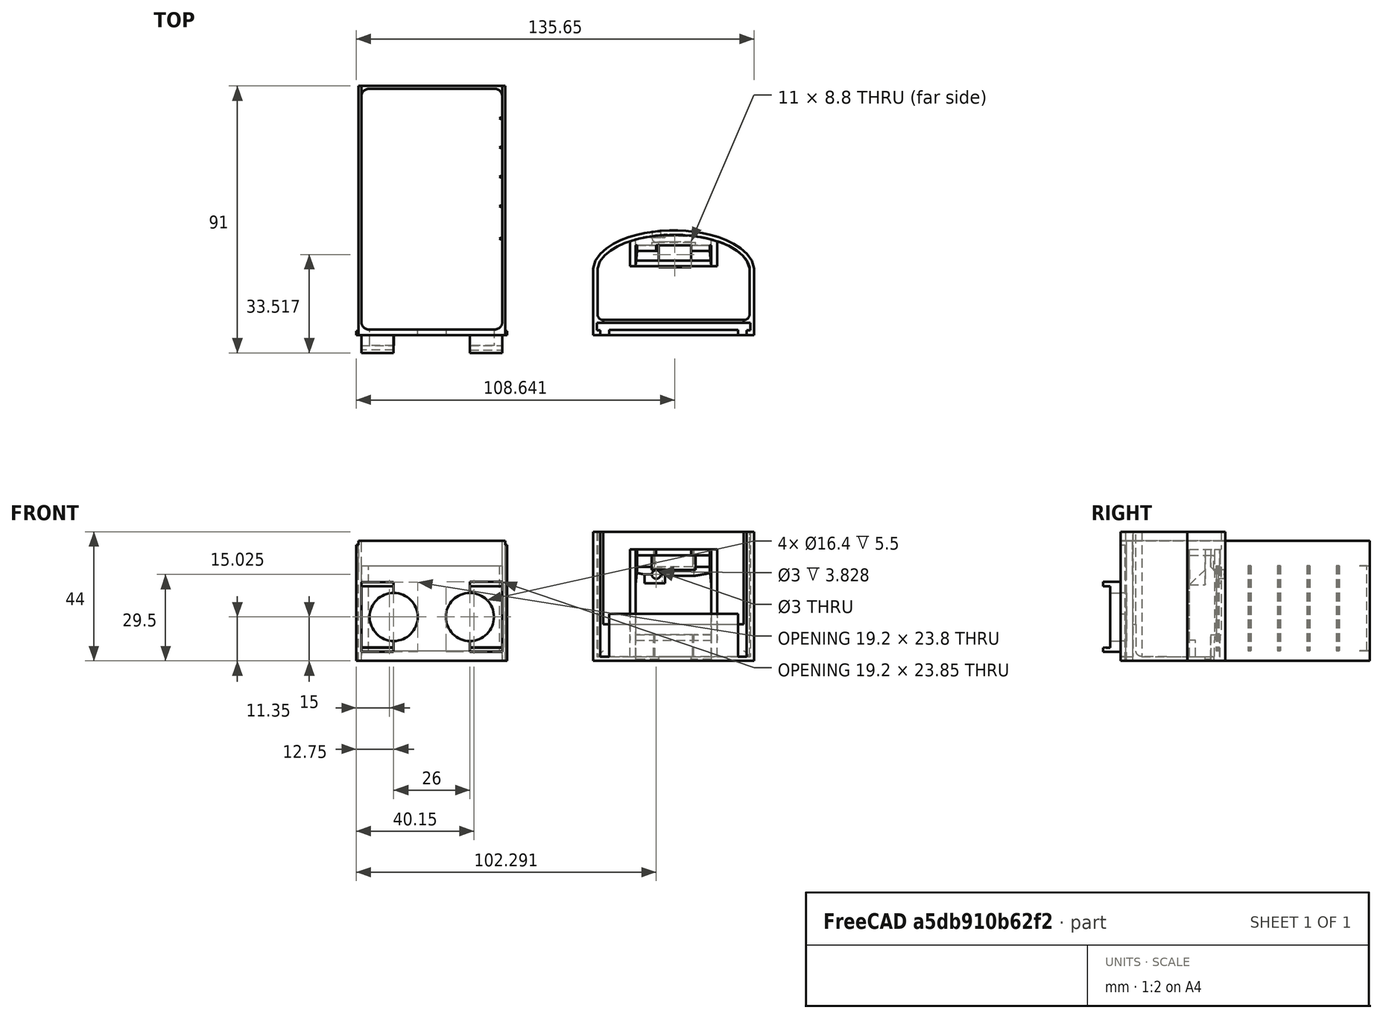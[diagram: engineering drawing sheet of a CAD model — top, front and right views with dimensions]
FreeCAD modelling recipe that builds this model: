
FCSTD DOCUMENT  (FreeCAD 0.18.4R)
Label: sonic.sensor.V5
License: All rights reserved
LicenseURL: http://en.wikipedia.org/wiki/All_rights_reserved
objects: Part::Extrusion×56, Part::Feature×45, Part::Part2DObjectPython×29, Part::Cut×25, Part::MultiFuse×17, Part::FeaturePython×8, App::DocumentObjectGroup×4
note: 180 computed .brp shape members not serialized (recipe doc carries the construction recipe); baked Part::Feature solids carry a one-line shape summary decoded from their .brp

FEATURE [Part::Feature] Extrusion004
  Placement = pos=(0,4e-15,-3.5) rot=(0,0,1;0rad)
  shape: bbox 47.9 x 2.5 x 34.5 mm, 6 faces (baked)
FEATURE [Part::Part2DObjectPython] Rectangle007  # Draft 2D object (typed FeaturePython)
  ChamferSize = 0
  Columns = 1
  FilletRadius = 0
  Height = 2.5
  Length = 0.2
  MakeFace = true
  Placement = pos=(133.392,-28.2833,50) rot=(0,0,1;0rad)
  Rows = 1
FEATURE [Part::Part2DObjectPython] Rectangle  # Draft 2D object (typed FeaturePython)
  ChamferSize = 0
  Columns = 1
  FilletRadius = 0
  Height = 50
  Length = 54.9181
  MakeFace = true
  Placement = pos=(79.9819,-14.25,-6e-15) rot=(1,0,0;1.5708rad)
  Rows = 1
FEATURE [Part::Feature] Face
  shape: bbox 51.9 x 2e-07 x 45.5 mm, 1 faces, 0 solids (baked)
FEATURE [Part::Feature] Slice_child  label="Slice.003"
  Placement = pos=(0,5,0) rot=(0,0,1;0rad)
  shape: bbox 54.92 x 13.01 x 50 mm, 74 faces (baked)
FEATURE [Part::Extrusion] Extrusion
  Base = -> Rectangle
  Dir = (-1.25e-14,-15.75,-2.1e-14)
  DirMode = 0
  FaceMakerClass = Part::FaceMakerBullseye
  LengthFwd = 0
  LengthRev = 0
  Solid = true
  Symmetric = false
FEATURE [Part::Part2DObjectPython] Rectangle004  # Draft 2D object (typed FeaturePython)
  ChamferSize = 0
  Columns = 1
  FilletRadius = 0
  Height = 14.5
  Length = 43.9024
  MakeFace = true
  Placement = pos=(85.4897,-30,1.5) rot=(1,0,0;1.5708rad)
  Rows = 1
FEATURE [Part::Part2DObjectPython] Rectangle002  # Draft 2D object (typed FeaturePython)
  ChamferSize = 0
  Columns = 1
  FilletRadius = 0
  Height = 2.5
  Length = 51.9024
  MakeFace = true
  Placement = pos=(81.4897,-25.7833,47) rot=(0,0,1;0rad)
  Rows = 1
FEATURE [Part::Extrusion] Extrusion002
  Base = -> Rectangle002
  Dir = (0,9.1e-14,-45.5)
  DirMode = 0
  FaceMakerClass = Part::FaceMakerBullseye
  LengthFwd = 0
  LengthRev = 0
  Solid = true
  Symmetric = false
FEATURE [Part::Cut] Cut001
  Base = -> Extrusion002
  Tool = -> Extrusion004
FEATURE [Part::Part2DObjectPython] Rectangle005  # Draft 2D object (typed FeaturePython)
  ChamferSize = 0
  Columns = 1
  FilletRadius = 0
  Height = 1.71667
  Length = 1
  MakeFace = true
  Placement = pos=(132.392,-30,47) rot=(0,0,1;0rad)
  Rows = 1
FEATURE [Part::Extrusion] Extrusion007
  Base = -> Rectangle005
  Dir = (-1.616e-13,1.397e-13,-45.5)
  DirMode = 0
  FaceMakerClass = Part::FaceMakerBullseye
  LengthFwd = 0
  LengthRev = 0
  Solid = true
  Symmetric = false
FEATURE [Part::Extrusion] Extrusion006
  Base = -> Rectangle004
  Dir = (-1.38e-14,1.81667,-9.5e-15)
  DirMode = 0
  FaceMakerClass = Part::FaceMakerBullseye
  LengthFwd = 0
  LengthRev = 0
  Solid = true
  Symmetric = false
FEATURE [Part::Extrusion] Extrusion005
  Base = -> Face
  Dir = (0,-1.5,-3e-15)
  DirMode = 0
  FaceMakerClass = Part::FaceMakerBullseye
  LengthFwd = 0
  LengthRev = 0
  Solid = true
  Symmetric = false
FEATURE [Part::Part2DObjectPython] Rectangle001  # Draft 2D object (typed FeaturePython)
  ChamferSize = 0
  Columns = 1
  FilletRadius = 0
  Height = 48.5
  Length = 51.9024
  MakeFace = true
  Placement = pos=(81.4897,-14.25,1.5) rot=(1,0,0;1.5708rad)
  Rows = 1
FEATURE [Part::Extrusion] Extrusion001
  Base = -> Rectangle001
  Dir = (-1.25e-14,-15.75,-2.1e-14)
  DirMode = 0
  FaceMakerClass = Part::FaceMakerBullseye
  LengthFwd = 0
  LengthRev = 0
  Solid = true
  Symmetric = false
FEATURE [Part::Cut] Cut
  Base = -> Extrusion
  Tool = -> Extrusion001
FEATURE [Part::Feature] Face001
  shape: bbox 54.92 x 2e-07 x 50 mm, 1 faces, 0 solids (baked)
FEATURE [Part::Feature] Extrusion010
  Placement = pos=(-52.1024,4.6e-14,-2.8e-14) rot=(0,0,1;0rad)
  shape: bbox 0.2 x 2.5 x 48.5 mm, 6 faces (baked)
FEATURE [Part::Cut] Cut002
  Base = -> Cut001
  Tool = -> Extrusion005
FEATURE [Part::MultiFuse] Fusion
  Shapes = -> [Cut,Cut002,Extrusion006]
FEATURE [Part::Part2DObjectPython] Rectangle006  # Draft 2D object (typed FeaturePython)
  ChamferSize = 0
  Columns = 1
  FilletRadius = 0
  Height = 1
  Length = 1.71667
  MakeFace = true
  Placement = pos=(81.4897,-28.2833,47) rot=(0,0,-1;1.5708rad)
  Rows = 1
FEATURE [Part::Extrusion] Extrusion008
  Base = -> Rectangle006
  Dir = (-4.87e-14,1.397e-13,-45.5)
  DirMode = 0
  FaceMakerClass = Part::FaceMakerBullseye
  LengthFwd = 0
  LengthRev = 0
  Solid = true
  Symmetric = false
FEATURE [Part::MultiFuse] Fusion001
  Shapes = -> [Fusion,Extrusion008,Extrusion007]
FEATURE [Part::Extrusion] Extrusion009
  Base = -> Rectangle007
  Dir = (0,7.3e-15,-48.5)
  DirMode = 0
  FaceMakerClass = Part::FaceMakerBullseye
  LengthFwd = 0
  LengthRev = 0
  Solid = true
  Symmetric = false
FEATURE [Part::Cut] Cut003
  Base = -> Fusion001
  Tool = -> Extrusion009
FEATURE [Part::Cut] Cut004
  Base = -> Cut003
  Tool = -> Extrusion010
FEATURE [Part::Part2DObjectPython] Rectangle009  # Draft 2D object (typed FeaturePython)
  ChamferSize = 0
  Columns = 1
  FilletRadius = 0
  Height = 2
  Length = 2
  MakeFace = true
  Placement = pos=(133.392,-22.7833,1.5) rot=(0.57735,-0.57735,-0.57735;2.0944rad)
  Rows = 1
FEATURE [Part::Extrusion] Extrusion011
  Base = -> Rectangle009
  Dir = (-51.9024,0,0)
  DirMode = 0
  FaceMakerClass = Part::FaceMakerBullseye
  LengthFwd = 0
  LengthRev = 0
  Solid = true
  Symmetric = false
FEATURE [Part::Part2DObjectPython] Circle  # Draft 2D object (typed FeaturePython)
  FirstAngle = 0
  LastAngle = 0
  MakeFace = true
  Placement = pos=(81.4897,-22.7833,3.5) rot=(0.57735,-0.57735,-0.57735;2.0944rad)
  Radius = 2
  Support = -> [Extrusion011]
FEATURE [Part::Extrusion] Extrusion012
  Base = -> Circle
  Dir = (51.9024,0,0)
  DirMode = 0
  FaceMakerClass = Part::FaceMakerBullseye
  LengthFwd = 0
  LengthRev = 0
  Solid = true
  Symmetric = false
FEATURE [Part::Cut] Cut005
  Base = -> Extrusion011
  Tool = -> Extrusion012
FEATURE [Part::MultiFuse] Fusion002
  Shapes = -> [Cut004,Cut005]
FEATURE [Part::Part2DObjectPython] Rectangle010  # Draft 2D object (typed FeaturePython)
  ChamferSize = 0
  Columns = 1
  FilletRadius = 0
  Height = 2.00245
  Length = 2
  MakeFace = true
  Placement = pos=(133.392,-24.7833,47) rot=(0,0,1;1.5708rad)
  Rows = 1
FEATURE [Part::Extrusion] Extrusion013
  Base = -> Rectangle010
  Dir = (1.161e-13,2.071e-13,-45.5)
  DirMode = 0
  FaceMakerClass = Part::FaceMakerBullseye
  LengthFwd = 0
  LengthRev = 0
  Solid = true
  Symmetric = false
FEATURE [Part::Part2DObjectPython] Circle001  # Draft 2D object (typed FeaturePython)
  FirstAngle = 0
  LastAngle = 0
  MakeFace = true
  Placement = pos=(131.39,-22.7833,47) rot=(0,0,1;1.5708rad)
  Radius = 2
  Support = -> [Extrusion013]
FEATURE [Part::Extrusion] Extrusion014
  Base = -> Circle001
  Dir = (3.53e-14,2.425e-13,-45.5)
  DirMode = 0
  FaceMakerClass = Part::FaceMakerBullseye
  LengthFwd = 0
  LengthRev = 0
  Solid = true
  Symmetric = false
FEATURE [Part::Cut] Cut006
  Base = -> Extrusion013
  Tool = -> Extrusion014
FEATURE [Part::Part2DObjectPython] Rectangle012  # Draft 2D object (typed FeaturePython)
  ChamferSize = 0
  Columns = 1
  FilletRadius = 0
  Height = 2
  Length = 2
  MakeFace = true
  Placement = pos=(83.4897,-24.7833,47) rot=(0,0,1;1.5708rad)
  Rows = 1
  Support = -> [Fusion002]
FEATURE [Part::Extrusion] Extrusion015
  Base = -> Rectangle012
  Dir = (1.161e-13,2.071e-13,-45.5)
  DirMode = 0
  FaceMakerClass = Part::FaceMakerBullseye
  LengthFwd = 0
  LengthRev = 0
  Solid = true
  Symmetric = false
FEATURE [Part::Part2DObjectPython] Circle002  # Draft 2D object (typed FeaturePython)
  FirstAngle = 0
  LastAngle = 0
  MakeFace = true
  Placement = pos=(83.4897,-22.7833,47) rot=(0,0,1;1.5708rad)
  Radius = 2
  Support = -> [Extrusion015]
FEATURE [Part::Extrusion] Extrusion016
  Base = -> Circle002
  Dir = (3.53e-14,2.425e-13,-45.5)
  DirMode = 0
  FaceMakerClass = Part::FaceMakerBullseye
  LengthFwd = 0
  LengthRev = 0
  Solid = true
  Symmetric = false
FEATURE [Part::Cut] Cut007
  Base = -> Extrusion015
  Tool = -> Extrusion016
FEATURE [Part::MultiFuse] Fusion003
  Shapes = -> [Cut007,Fusion002,Cut006]
FEATURE [Part::Extrusion] Extrusion017
  Base = -> Face001
  Dir = (4e-15,5,6.7e-15)
  DirMode = 0
  FaceMakerClass = Part::FaceMakerBullseye
  LengthFwd = 0
  LengthRev = 0
  Solid = true
  Symmetric = false
FEATURE [Part::MultiFuse] Fusion004
  Shapes = -> [Fusion003,Extrusion017,Slice_child]
FEATURE [Part::Feature] Fusion016
  Placement = pos=(4e-15,0,-5) rot=(0,0,1;0rad)
  shape: bbox 51.5 x 71 x 41 mm, 89 faces (baked)
FEATURE [Part::Part2DObjectPython] Rectangle019  # Draft 2D object (typed FeaturePython)
  ChamferSize = 0
  Columns = 1
  FilletRadius = 0
  Height = 6
  Length = 11
  MakeFace = true
  Placement = pos=(38,-30,6.8002) rot=(1,0,0;3.14159rad)
  Rows = 1
  Support = -> [Fusion016]
FEATURE [Part::Extrusion] Extrusion025
  Base = -> Rectangle019
  Dir = (0,0,-0.699902)
  DirMode = 0
  FaceMakerClass = Part::FaceMakerBullseye
  LengthFwd = 0
  LengthRev = 0
  Solid = true
  Symmetric = false
FEATURE [Part::Part2DObjectPython] Rectangle020  # Draft 2D object (typed FeaturePython)
  ChamferSize = 0
  Columns = 1
  FilletRadius = 0
  Height = 11
  Length = 6
  MakeFace = true
  Placement = pos=(12,-30,6.8002) rot=(0.707107,-0.707107,0;3.14159rad)
  Rows = 1
  Support = -> [Fusion016]
FEATURE [Part::Extrusion] Extrusion026
  Base = -> Rectangle020
  Dir = (0,0,-0.699902)
  DirMode = 0
  FaceMakerClass = Part::FaceMakerBullseye
  LengthFwd = 0
  LengthRev = 0
  Solid = true
  Symmetric = false
FEATURE [Part::Part2DObjectPython] Rectangle021  # Draft 2D object (typed FeaturePython)
  ChamferSize = 0
  Columns = 1
  FilletRadius = 0
  Height = 6
  Length = 11
  MakeFace = true
  Placement = pos=(49,-30,29.2) rot=(0,0,1;3.14159rad)
  Rows = 1
  Support = -> [Fusion016]
FEATURE [Part::Part2DObjectPython] Rectangle022  # Draft 2D object (typed FeaturePython)
  ChamferSize = 0
  Columns = 1
  FilletRadius = 0
  Height = 6
  Length = 11
  MakeFace = true
  Placement = pos=(12,-30,29.2) rot=(0,0,1;3.14159rad)
  Rows = 1
FEATURE [Part::Extrusion] Extrusion027
  Base = -> Rectangle022
  Dir = (0,0,0.699902)
  DirMode = 0
  FaceMakerClass = Part::FaceMakerBullseye
  LengthFwd = 0
  LengthRev = 0
  Solid = true
  Symmetric = false
FEATURE [Part::Extrusion] Extrusion028
  Base = -> Rectangle021
  Dir = (0,0,0.749176)
  DirMode = 0
  FaceMakerClass = Part::FaceMakerBullseye
  LengthFwd = 0
  LengthRev = 0
  Solid = true
  Symmetric = false
FEATURE [Part::MultiFuse] Fusion017
  Shapes = -> [Extrusion026,Extrusion025,Extrusion028,Extrusion027]
FEATURE [Part::MultiFuse] Fusion018
  Shapes = -> [Fusion016,Fusion017]
FEATURE [Part::Feature] Face002
  Placement = pos=(0,5,0) rot=(0,0,1;0rad)
  shape: bbox 1.002e-05 x 1.2 x 0.75 mm, 1 faces, 0 solids (baked)
FEATURE [Part::Extrusion] Extrusion029
  Base = -> Face002
  Dir = (0.2,0,0)
  DirMode = 0
  FaceMakerClass = Part::FaceMakerBullseye
  LengthFwd = 0
  LengthRev = 0
  Solid = true
  Symmetric = false
FEATURE [Part::Cut] Cut031
  Base = -> Fusion004
  Tool = -> Extrusion029
FEATURE [Part::Feature] Face003
  Placement = pos=(0,5,0) rot=(0,0,1;0rad)
  shape: bbox 1.002e-05 x 1.2 x 0.75 mm, 1 faces, 0 solids (baked)
FEATURE [Part::Extrusion] Extrusion030
  Base = -> Face003
  Dir = (-0.2,0,0)
  DirMode = 0
  FaceMakerClass = Part::FaceMakerBullseye
  LengthFwd = 0
  LengthRev = 0
  Solid = true
  Symmetric = false
FEATURE [Part::Cut] Cut032
  Base = -> Cut031
  Tool = -> Extrusion030
FEATURE [Part::Feature] Face004
  shape: bbox 8.9 x 1.8 x 1.002e-05 mm, 1 faces, 0 solids (baked)
FEATURE [Part::Extrusion] Extrusion031
  Base = -> Face004
  Dir = (0,0,-0.2)
  DirMode = 0
  FaceMakerClass = Part::FaceMakerBullseye
  LengthFwd = 0
  LengthRev = 0
  Solid = true
  Symmetric = false
FEATURE [Part::Cut] Cut033
  Base = -> Cut032
  Tool = -> Extrusion031
FEATURE [Part::Feature] Face005
  shape: bbox 0.2 x 1.2 x 1.002e-05 mm, 1 faces, 0 solids (baked)
FEATURE [Part::Extrusion] Extrusion032
  Base = -> Face005
  Dir = (0,0,-0.2)
  DirMode = 0
  FaceMakerClass = Part::FaceMakerBullseye
  LengthFwd = 0
  LengthRev = 0
  Solid = true
  Symmetric = false
FEATURE [Part::Cut] Cut034
  Base = -> Cut033
  Tool = -> Extrusion032
FEATURE [Part::Feature] Face006
  shape: bbox 8 x 1.8 x 1.002e-05 mm, 1 faces, 0 solids (baked)
FEATURE [Part::Extrusion] Extrusion033
  Base = -> Face006
  Dir = (0,0,-0.2)
  DirMode = 0
  FaceMakerClass = Part::FaceMakerBullseye
  LengthFwd = 0
  LengthRev = 0
  Solid = true
  Symmetric = false
FEATURE [Part::Cut] Cut035
  Base = -> Cut034
  Tool = -> Extrusion033
FEATURE [Part::Feature] Face007
  shape: bbox 0.2 x 1.2 x 1.002e-05 mm, 1 faces, 0 solids (baked)
FEATURE [Part::Extrusion] Extrusion034
  Base = -> Face007
  Dir = (0,0,-0.2)
  DirMode = 0
  FaceMakerClass = Part::FaceMakerBullseye
  LengthFwd = 0
  LengthRev = 0
  Solid = true
  Symmetric = false
FEATURE [Part::Cut] Cut036
  Base = -> Cut035
  Tool = -> Extrusion034
FEATURE [Part::Feature] Face008
  shape: bbox 8 x 1.002e-05 x 0.75 mm, 1 faces, 0 solids (baked)
FEATURE [Part::Extrusion] Extrusion035
  Base = -> Face008
  Dir = (0,-0.2,0)
  DirMode = 0
  FaceMakerClass = Part::FaceMakerBullseye
  LengthFwd = 0
  LengthRev = 0
  Solid = true
  Symmetric = false
FEATURE [Part::Feature] Face009
  shape: bbox 8 x 1.002e-05 x 0.2 mm, 1 faces, 0 solids (baked)
FEATURE [Part::Extrusion] Extrusion036
  Base = -> Face009
  Dir = (0,-0.2,0)
  DirMode = 0
  FaceMakerClass = Part::FaceMakerBullseye
  LengthFwd = 0
  LengthRev = 0
  Solid = true
  Symmetric = false
FEATURE [Part::Cut] Cut037
  Base = -> Cut036
  Tool = -> Extrusion035
FEATURE [Part::Cut] Cut038
  Base = -> Cut037
  Tool = -> Extrusion036
FEATURE [Part::Feature] Face010
  shape: bbox 8.9 x 1.002e-05 x 0.75 mm, 1 faces, 0 solids (baked)
FEATURE [Part::Extrusion] Extrusion037
  Base = -> Face010
  Dir = (0,-0.2,0)
  DirMode = 0
  FaceMakerClass = Part::FaceMakerBullseye
  LengthFwd = 0
  LengthRev = 0
  Solid = true
  Symmetric = false
FEATURE [Part::Feature] Face011
  shape: bbox 8.9 x 1.002e-05 x 0.2 mm, 1 faces, 0 solids (baked)
FEATURE [Part::Extrusion] Extrusion038
  Base = -> Face011
  Dir = (0,-0.2,0)
  DirMode = 0
  FaceMakerClass = Part::FaceMakerBullseye
  LengthFwd = 0
  LengthRev = 0
  Solid = true
  Symmetric = false
FEATURE [Part::Cut] Cut039
  Base = -> Cut038
  Tool = -> Extrusion037
FEATURE [Part::Cut] Cut040
  Base = -> Cut039
  Tool = -> Extrusion038
FEATURE [Part::Part2DObjectPython] Rectangle023  # Draft 2D object (typed FeaturePython)
  ChamferSize = 0
  Columns = 1
  FilletRadius = 0
  Height = 1.5
  Length = 0.75
  MakeFace = true
  Placement = pos=(-0.75,-30,41) rot=(0,0,1;0rad)
  Rows = 1
  Support = -> [Fusion018]
FEATURE [Part::Part2DObjectPython] Rectangle024  # Draft 2D object (typed FeaturePython)
  ChamferSize = 0
  Columns = 1
  FilletRadius = 0
  Height = 1.5
  Length = 0.75
  MakeFace = true
  Placement = pos=(50,-30,41) rot=(0,0,1;0rad)
  Rows = 1
FEATURE [Part::Extrusion] Extrusion039
  Base = -> Rectangle024
  Dir = (0,0,-1)
  DirMode = 0
  FaceMakerClass = Part::FaceMakerBullseye
  LengthFwd = 0
  LengthRev = 0
  Solid = true
  Symmetric = false
FEATURE [Part::Extrusion] Extrusion040
  Base = -> Rectangle023
  Dir = (0,0,-1)
  DirMode = 0
  FaceMakerClass = Part::FaceMakerBullseye
  LengthFwd = 0
  LengthRev = 0
  Solid = true
  Symmetric = false
FEATURE [Part::Cut] Cut041
  Base = -> Fusion018
  Tool = -> Extrusion039
FEATURE [Part::Cut] Cut042
  Base = -> Cut041
  Tool = -> Extrusion040
FEATURE [Part::Part2DObjectPython] Rectangle026  # Draft 2D object (typed FeaturePython)
  ChamferSize = 0
  Columns = 1
  FilletRadius = 0
  Height = 79.8861
  Length = 72.5841
  MakeFace = true
  Placement = pos=(-10.6149,-28,32.5) rot=(0,0,1;0rad)
  Rows = 1
  Support = -> [Cut042]
FEATURE [Part::Extrusion] Extrusion041
  Base = -> Rectangle026
  Dir = (0,0,70.6218)
  DirMode = 0
  FaceMakerClass = Part::FaceMakerBullseye
  LengthFwd = 0
  LengthRev = 0
  Solid = true
  Symmetric = false
FEATURE [Part::Cut] Cut043
  Base = -> Cut042
  Tool = -> Extrusion041
FEATURE [Part::Part2DObjectPython] Rectangle028  # Draft 2D object (typed FeaturePython)
  ChamferSize = 0
  Columns = 1
  FilletRadius = 0
  Height = 277.459
  Length = 179.893
  MakeFace = true
  Placement = pos=(-88.9464,2.9782,-138.729) rot=(1,0,0;1.5708rad)
  Rows = 1
  Support = -> [Cut043]
FEATURE [Part::FeaturePython] Slice  # WARN: FeaturePython — macro-defined, semantics opaque (R4)
  Base = -> Cut043
  Mode = 1
  Tolerance = 0
  Tools = -> [Rectangle028]
FEATURE [Part::FeaturePython] Slice_child0  label="Slice.0"  # WARN: FeaturePython — macro-defined, semantics opaque (R4)
  Base = -> Slice
  FilterType = 1
  Invert = false
  OverrideMaxVal = 0
  WindowFrom = 80
  WindowTo = 100
  items = 0
FEATURE [Part::Feature] Slice_child002  label="Slice.004"
  Placement = pos=(0,20,0) rot=(0,0,1;0rad)
  shape: bbox 50 x 32.02 x 32.5 mm, 17 faces (baked)
FEATURE [Part::Feature] Face012
  shape: bbox 1 x 6.243e-07 x 32.5 mm, 1 faces, 0 solids (baked)
FEATURE [Part::Extrusion] Extrusion042
  Base = -> Face012
  Dir = (6e-16,20,-4.4e-15)
  DirMode = 0
  FaceMakerClass = Part::FaceMakerBullseye
  LengthFwd = 0
  LengthRev = 0
  Solid = true
  Symmetric = false
FEATURE [Part::Feature] Face013
  shape: bbox 1 x 6.243e-07 x 32.5 mm, 1 faces, 0 solids (baked)
FEATURE [Part::Extrusion] Extrusion043
  Base = -> Face013
  Dir = (6e-16,20,-4.4e-15)
  DirMode = 0
  FaceMakerClass = Part::FaceMakerBullseye
  LengthFwd = 0
  LengthRev = 0
  Solid = true
  Symmetric = false
FEATURE [Part::MultiFuse] Fusion019
  Shapes = -> [Slice_child0,Extrusion042,Extrusion043,Slice_child002]
FEATURE [Part::Part2DObjectPython] Wire002  # Draft 2D object (typed FeaturePython)
  ChamferSize = 0
  Closed = true
  End = (49,43.5,32.5)
  FilletRadius = 0
  Length = 3.23607
  MakeFace = true
  Placement = pos=(49,44.5,32.5) rot=(0,0,1;0rad)
  Points = (3) [(0,0,0),(-1,-0.5,0),(0,-1,0)]
  Start = (49,44.5,32.5)
  Subdivisions = 0
FEATURE [Part::Extrusion] Extrusion044
  Base = -> Wire002
  Dir = (0,0,-32.5)
  DirMode = 0
  FaceMakerClass = Part::FaceMakerBullseye
  LengthFwd = 0
  LengthRev = 0
  Solid = true
  Symmetric = false
FEATURE [Part::Feature] Extrusion045
  Placement = pos=(7.1e-15,-10,-7.1e-15) rot=(0,0,1;0rad)
  shape: bbox 1 x 1 x 32.5 mm, 5 faces (baked)
FEATURE [Part::Feature] Extrusion046
  Placement = pos=(0,-30,0) rot=(0,0,1;0rad)
  shape: bbox 1 x 1 x 32.5 mm, 5 faces (baked)
FEATURE [Part::Feature] Extrusion047
  Placement = pos=(-7.1e-15,-20,7.1e-15) rot=(0,0,1;0rad)
  shape: bbox 1 x 1 x 32.5 mm, 5 faces (baked)
FEATURE [Part::Feature] Extrusion048
  Placement = pos=(-7.1e-15,-41.0218,7.1e-15) rot=(0,0,1;0rad)
  shape: bbox 1 x 1 x 32.5 mm, 5 faces (baked)
FEATURE [Part::MultiFuse] Fusion020
  Shapes = -> [Extrusion048,Extrusion046,Extrusion047,Extrusion045,Extrusion044,Fusion019]
FEATURE [Part::Feature] Face014
  shape: bbox 1 x 32.02 x 6.243e-07 mm, 1 faces, 0 solids (baked)
FEATURE [Part::Extrusion] Extrusion049
  Base = -> Face014
  Dir = (0,0,8.5)
  DirMode = 0
  FaceMakerClass = Part::FaceMakerBullseye
  LengthFwd = 0
  LengthRev = 0
  Solid = true
  Symmetric = false
FEATURE [Part::Feature] Face015
  shape: bbox 1 x 20 x 6.243e-07 mm, 1 faces, 0 solids (baked)
FEATURE [Part::Extrusion] Extrusion050
  Base = -> Face015
  Dir = (0,1.9e-15,8.5)
  DirMode = 0
  FaceMakerClass = Part::FaceMakerBullseye
  LengthFwd = 0
  LengthRev = 0
  Solid = true
  Symmetric = false
FEATURE [Part::Feature] Face016
  shape: bbox 3.5 x 30.98 x 6.243e-07 mm, 1 faces, 0 solids (baked)
FEATURE [Part::Extrusion] Extrusion051
  Base = -> Face016
  Dir = (0,0,8.5)
  DirMode = 0
  FaceMakerClass = Part::FaceMakerBullseye
  LengthFwd = 0
  LengthRev = 0
  Solid = true
  Symmetric = false
FEATURE [Part::Feature] Face017
  shape: bbox 3.453 x 30.98 x 6.243e-07 mm, 1 faces, 0 solids (baked)
FEATURE [Part::Extrusion] Extrusion052
  Base = -> Face017
  Dir = (0,0,8.5)
  DirMode = 0
  FaceMakerClass = Part::FaceMakerBullseye
  LengthFwd = 0
  LengthRev = 0
  Solid = true
  Symmetric = false
FEATURE [Part::Feature] Face018
  shape: bbox 1 x 20 x 6.243e-07 mm, 1 faces, 0 solids (baked)
FEATURE [Part::Extrusion] Extrusion053
  Base = -> Face018
  Dir = (0,1.9e-15,8.5)
  DirMode = 0
  FaceMakerClass = Part::FaceMakerBullseye
  LengthFwd = 0
  LengthRev = 0
  Solid = true
  Symmetric = false
FEATURE [Part::Feature] Face019
  shape: bbox 1 x 32.02 x 6.243e-07 mm, 1 faces, 0 solids (baked)
FEATURE [Part::Extrusion] Extrusion054
  Base = -> Face019
  Dir = (0,0,8.5)
  DirMode = 0
  FaceMakerClass = Part::FaceMakerBullseye
  LengthFwd = 0
  LengthRev = 0
  Solid = true
  Symmetric = false
FEATURE [Part::Part2DObjectPython] Rectangle030  # Draft 2D object (typed FeaturePython)
  ChamferSize = 0
  Columns = 1
  FilletRadius = 0
  Height = 57.6888
  Length = 133.549
  MakeFace = true
  Placement = pos=(-65.7746,-25.5,-16.6888) rot=(1,0,0;1.5708rad)
  Rows = 1
  Support = -> [Fusion020]
FEATURE [Part::MultiFuse] Fusion021
  Shapes = -> [Fusion020,Extrusion054,Extrusion053,Extrusion052,Extrusion049,Extrusion050,Extrusion051]
FEATURE [App::DocumentObjectGroup] GrExplode_Slice  label="Exploded Slice"
  Group = -> [Fusion021]
FEATURE [Part::FeaturePython] Slice001  # WARN: FeaturePython — macro-defined, semantics opaque (R4)
  Base = -> Fusion021
  Mode = 1
  Tolerance = 0
  Tools = -> [Rectangle030]
FEATURE [Part::FeaturePython] Slice001_child0  label="Slice001.0"  # WARN: FeaturePython — macro-defined, semantics opaque (R4)
  Base = -> Slice001
  FilterType = 1
  Invert = false
  OverrideMaxVal = 0
  WindowFrom = 80
  WindowTo = 100
  items = 0
FEATURE [Part::Feature] Slice001_child  label="Slice001.002"
  Placement = pos=(0,0,-3) rot=(0,0,1;0rad)
  shape: bbox 51.5 x 10.5 x 41 mm, 99 faces (baked)
FEATURE [Part::Feature] Face020
  Placement = pos=(0,0,-3) rot=(0,0,1;0rad)
  shape: bbox 3.453 x 2.5 x 6.243e-07 mm, 1 faces, 0 solids (baked)
FEATURE [Part::Extrusion] Extrusion055
  Base = -> Face020
  Dir = (0,0,3)
  DirMode = 0
  FaceMakerClass = Part::FaceMakerBullseye
  LengthFwd = 0
  LengthRev = 0
  Solid = true
  Symmetric = false
FEATURE [Part::Feature] Face021
  Placement = pos=(0,0,-3) rot=(0,0,1;0rad)
  shape: bbox 50 x 2 x 6.243e-07 mm, 1 faces, 0 solids (baked)
FEATURE [Part::Extrusion] Extrusion056
  Base = -> Face021
  Dir = (0,0,3)
  DirMode = 0
  FaceMakerClass = Part::FaceMakerBullseye
  LengthFwd = 0
  LengthRev = 0
  Solid = true
  Symmetric = false
FEATURE [Part::Feature] Face022
  Placement = pos=(0,0,-3) rot=(0,0,1;0rad)
  shape: bbox 3.5 x 2.5 x 6.243e-07 mm, 1 faces, 0 solids (baked)
FEATURE [Part::Extrusion] Extrusion057
  Base = -> Face022
  Dir = (0,0,3)
  DirMode = 0
  FaceMakerClass = Part::FaceMakerBullseye
  LengthFwd = 0
  LengthRev = 0
  Solid = true
  Symmetric = false
FEATURE [Part::Feature] Face023
  Placement = pos=(-0.75,-30,37) rot=(0,0,1;0rad)
  shape: bbox 0.75 x 1.5 x 5.243e-07 mm, 1 faces, 0 solids (baked)
FEATURE [Part::Extrusion] Extrusion058
  Base = -> Face023
  Dir = (0,0,2.5)
  DirMode = 0
  FaceMakerClass = Part::FaceMakerBullseye
  LengthFwd = 0
  LengthRev = 0
  Solid = true
  Symmetric = false
FEATURE [Part::Feature] Face024
  Placement = pos=(50,-30,37) rot=(0,0,1;0rad)
  shape: bbox 0.75 x 1.5 x 5.243e-07 mm, 1 faces, 0 solids (baked)
FEATURE [Part::Extrusion] Extrusion059
  Base = -> Face024
  Dir = (0,0,2.5)
  DirMode = 0
  FaceMakerClass = Part::FaceMakerBullseye
  LengthFwd = 0
  LengthRev = 0
  Solid = true
  Symmetric = false
FEATURE [Part::Part2DObjectPython] Rectangle031  # Draft 2D object (typed FeaturePython)
  ChamferSize = 0
  Columns = 1
  FilletRadius = 0
  Height = 97.2757
  Length = 71.9763
  MakeFace = true
  Placement = pos=(54.3318,-57.4008,-8.3e-14) rot=(0,1,0;3.14159rad)
  Rows = 1
  Support = -> [Slice001_child0]
FEATURE [Part::FeaturePython] Slice002  # WARN: FeaturePython — macro-defined, semantics opaque (R4)
  Base = -> Slice001_child
  Mode = 1
  Tolerance = 0
  Tools = -> [Rectangle031]
FEATURE [App::DocumentObjectGroup] GrExplode_Slice002  label="Exploded Slice002"
FEATURE [Part::FeaturePython] Slice002_child0  label="Slice002.0"  # WARN: FeaturePython — macro-defined, semantics opaque (R4)
  Base = -> Slice002
  FilterType = 1
  Invert = false
  OverrideMaxVal = 0
  WindowFrom = 80
  WindowTo = 100
  items = 0
FEATURE [Part::Part2DObjectPython] Rectangle033  # Draft 2D object (typed FeaturePython)
  ChamferSize = 0
  Columns = 1
  FilletRadius = 0
  Height = 42.326
  Length = 62.0555
  MakeFace = true
  Placement = pos=(49,-10.5555,3.5) rot=(-0.57735,-0.57735,0.57735;2.0944rad)
  Rows = 1
  Support = -> [Slice001_child0]
FEATURE [Part::Extrusion] Extrusion060
  Base = -> Rectangle033
  Dir = (-23.995,0,0)
  DirMode = 0
  FaceMakerClass = Part::FaceMakerBullseye
  LengthFwd = 0
  LengthRev = 0
  Solid = true
  Symmetric = false
FEATURE [Part::Cut] Cut044
  Base = -> Slice001_child0
  Tool = -> Extrusion060
FEATURE [Part::MultiFuse] Fusion022
  Shapes = -> [Slice002_child0,Cut044]
FEATURE [Part::MultiFuse] Fusion023
  Shapes = -> [Extrusion056,Fusion022]
FEATURE [Part::MultiFuse] Fusion024
  Shapes = -> [Extrusion055,Extrusion059,Fusion023]
FEATURE [Part::MultiFuse] Fusion025
  Shapes = -> [Extrusion057,Extrusion058,Fusion024]
FEATURE [App::DocumentObjectGroup] GrExplode_Slice001  label="Exploded Slice001"
  Group = -> [Fusion025]
FEATURE [Part::Feature] Fusion025001  label="Fusion026"
  shape: bbox 51.5 x 91 x 41 mm, 79 faces (baked)
FEATURE [Part::Part2DObjectPython] Rectangle034  # Draft 2D object (typed FeaturePython)
  ChamferSize = 0
  Columns = 1
  FilletRadius = 0
  Height = 71.8194
  Length = 83.4407
  MakeFace = true
  Placement = pos=(70.4298,-57.3145,50) rot=(0,0,1;0rad)
  Rows = 1
  Support = -> [Cut040]
FEATURE [Part::Extrusion] Extrusion061
  Base = -> Rectangle034
  Dir = (0,9e-16,-6)
  DirMode = 0
  FaceMakerClass = Part::FaceMakerBullseye
  LengthFwd = 0
  LengthRev = 0
  Solid = true
  Symmetric = false
FEATURE [Part::Part2DObjectPython] Rectangle036  # Draft 2D object (typed FeaturePython)
  ChamferSize = 0
  Columns = 1
  FilletRadius = 0
  Height = 330.798
  Length = 264.085
  MakeFace = true
  Placement = pos=(-50.553,-14.25,-121.399) rot=(1,0,0;1.5708rad)
  Rows = 1
FEATURE [Part::Cut] Cut045
  Base = -> Cut040
  Tool = -> Extrusion061
FEATURE [Part::FeaturePython] Slice003  # WARN: FeaturePython — macro-defined, semantics opaque (R4)
  Base = -> Cut045
  Mode = 1
  Tolerance = 0
  Tools = -> [Rectangle036]
FEATURE [Part::FeaturePython] Slice003_child1  label="Slice003.1"  # WARN: FeaturePython — macro-defined, semantics opaque (R4)
  Base = -> Slice003
  FilterType = 1
  Invert = false
  OverrideMaxVal = 0
  WindowFrom = 80
  WindowTo = 100
  items = 1
FEATURE [Part::Feature] Slice003_child  label="Slice003.002"
  Placement = pos=(0,2,0) rot=(0,0,1;0rad)
  shape: bbox 54.92 x 18 x 44 mm, 100 faces (baked)
FEATURE [Part::Feature] Face025
  shape: bbox 54.92 x 3e-07 x 44 mm, 1 faces, 0 solids (baked)
FEATURE [Part::Extrusion] Extrusion062
  Base = -> Face025
  Dir = (2.1e-15,2,2.2e-15)
  DirMode = 0
  FaceMakerClass = Part::FaceMakerBullseye
  LengthFwd = 0
  LengthRev = 0
  Solid = true
  Symmetric = false
FEATURE [Part::MultiFuse] Fusion025002
  Shapes = -> [Slice003_child1,Extrusion062,Slice003_child]
FEATURE [Part::Part2DObjectPython] Rectangle037  # Draft 2D object (typed FeaturePython)
  ChamferSize = 0
  Columns = 1
  FilletRadius = 0
  Height = 7.8
  Length = 10
  MakeFace = true
  Placement = pos=(102.891,1.41667,-6e-15) rot=(1,0,0;3.14159rad)
  Rows = 1
FEATURE [Part::Extrusion] Extrusion063
  Base = -> Rectangle037
  Dir = (0,2e-16,1.5)
  DirMode = 0
  FaceMakerClass = Part::FaceMakerBullseye
  LengthFwd = 0
  LengthRev = 0
  Solid = true
  Symmetric = false
FEATURE [Part::Cut] Cut046
  Base = -> Fusion025002
  Tool = -> Extrusion063
FEATURE [Part::Feature] Face026
  Placement = pos=(0,7,0) rot=(0,0,1;0rad)
  shape: bbox 4 x 0.8114 x 1e-05 mm, 1 faces, 0 solids (baked)
FEATURE [Part::Extrusion] Extrusion064
  Base = -> Face026
  Dir = (0,0,-1)
  DirMode = 0
  FaceMakerClass = Part::FaceMakerBullseye
  LengthFwd = 0
  LengthRev = 0
  Solid = true
  Symmetric = false
FEATURE [Part::Feature] Face027
  Placement = pos=(0,7,0) rot=(0,0,1;0rad)
  shape: bbox 1.012e-05 x 0.8114 x 4 mm, 1 faces, 0 solids (baked)
FEATURE [Part::Extrusion] Extrusion065
  Base = -> Face027
  Dir = (1,0,0)
  DirMode = 0
  FaceMakerClass = Part::FaceMakerBullseye
  LengthFwd = 0
  LengthRev = 0
  Solid = true
  Symmetric = false
FEATURE [Part::Feature] Face028
  shape: bbox 1e-05 x 0.8114 x 1 mm, 1 faces, 0 solids (baked)
FEATURE [Part::Extrusion] Extrusion066
  Base = -> Face028
  Dir = (1,0,0)
  DirMode = 0
  FaceMakerClass = Part::FaceMakerBullseye
  LengthFwd = 0
  LengthRev = 0
  Solid = true
  Symmetric = false
FEATURE [Part::Feature] Face033
  Placement = pos=(0,7,0) rot=(0,0,1;0rad)
  shape: bbox 1e-05 x 0.3708 x 2 mm, 1 faces, 0 solids (baked)
FEATURE [Part::Extrusion] Extrusion067
  Base = -> Face033
  Dir = (-2,0,-1e-16)
  DirMode = 0
  FaceMakerClass = Part::FaceMakerBullseye
  LengthFwd = 0
  LengthRev = 0
  Solid = true
  Symmetric = false
FEATURE [Part::Feature] Face034
  shape: bbox 1e-05 x 0.3708 x 1 mm, 1 faces, 0 solids (baked)
FEATURE [Part::Extrusion] Extrusion068
  Base = -> Face034
  Dir = (-2,0,-1e-16)
  DirMode = 0
  FaceMakerClass = Part::FaceMakerBullseye
  LengthFwd = 0
  LengthRev = 0
  Solid = true
  Symmetric = false
FEATURE [Part::MultiFuse] Fusion025003
  Shapes = -> [Extrusion068,Extrusion064,Extrusion066,Extrusion065,Extrusion067]
FEATURE [Part::MultiFuse] Fusion025004
  Shapes = -> [Fusion025003,Cut046]
FEATURE [Part::Part2DObjectPython] Rectangle038  # Draft 2D object (typed FeaturePython)
  ChamferSize = 0
  Columns = 1
  FilletRadius = 0
  Height = 8.8
  Length = 11
  MakeFace = true
  Placement = pos=(102.391,1.91667,-7e-15) rot=(1,0,0;3.14159rad)
  Rows = 1
FEATURE [Part::Extrusion] Extrusion069
  Base = -> Rectangle038
  Dir = (0,2e-16,1.5)
  DirMode = 0
  FaceMakerClass = Part::FaceMakerBullseye
  LengthFwd = 0
  LengthRev = 0
  Solid = true
  Symmetric = false
FEATURE [Part::Cut] Cut047
  Base = -> Fusion025004
  Tool = -> Extrusion069
FEATURE [App::DocumentObjectGroup] GrExplode_Slice003  label="Exploded Slice003"
  Group = -> [Cut047]
FEATURE [Part::Feature] Cut047001  label="Cut048"
  shape: bbox 54.92 x 35.75 x 44 mm, 100 faces (baked)
FEATURE [Part::Feature] Fusion025001001  label="Fusion025007"
  shape: bbox 51.5 x 91 x 41 mm, 79 faces (baked)
